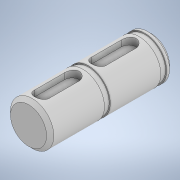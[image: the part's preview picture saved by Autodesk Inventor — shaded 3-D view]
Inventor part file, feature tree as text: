
AUTODESK INVENTOR PART (.ipt)
format: ipt  version: 2020 (Build 240168000, 168)  size: 260,608 bytes
history: native  units: mm
features: revolve x2, sketch x2, projected_geometry x2, plane x1, extrude x1, chamfer x1
ambient origin geometry x8: Origin, YZ Plane, XZ Plane, XY Plane, X Axis, Y Axis, Z Axis, Center Point
bodies: Solid1 (feature_tree)
feature tree (9):
  revolve  "Revolution1"  [1 undecoded]
  revolve  "Revolution2"  Angle=90.0deg
  plane  "Work Plane2"
  extrude  "Extrusion2"  Depth=6.15mm
  chamfer  "Chamfer3"  Distance=1.0mm
  sketch  "Sketch1"  dims[d0=3.0mm d1=17.0mm]
  sketch  "Sketch2"  dims[d2=90.0deg d4=90.0deg d49=6.15mm d50=1.0mm d52=1.0mm d53=0.0mm d54=0.5mm d55=2.0mm d56=45.0deg d58=7.0mm d60=3.5mm d61=3.5mm d71=0.9mm d72=2.85mm d73=0.8mm d74=1.0mm d75=1.0mm d77=6.15mm d78=1.5mm]
  projected_geometry  "Projected Loop4"
  projected_geometry  "Projected Loop5"
note: 1 required parameter value undecoded (feature->parameter linkage not recoverable at this tier; creation-order binding heuristic only, values carry confidence <= 0.55)
